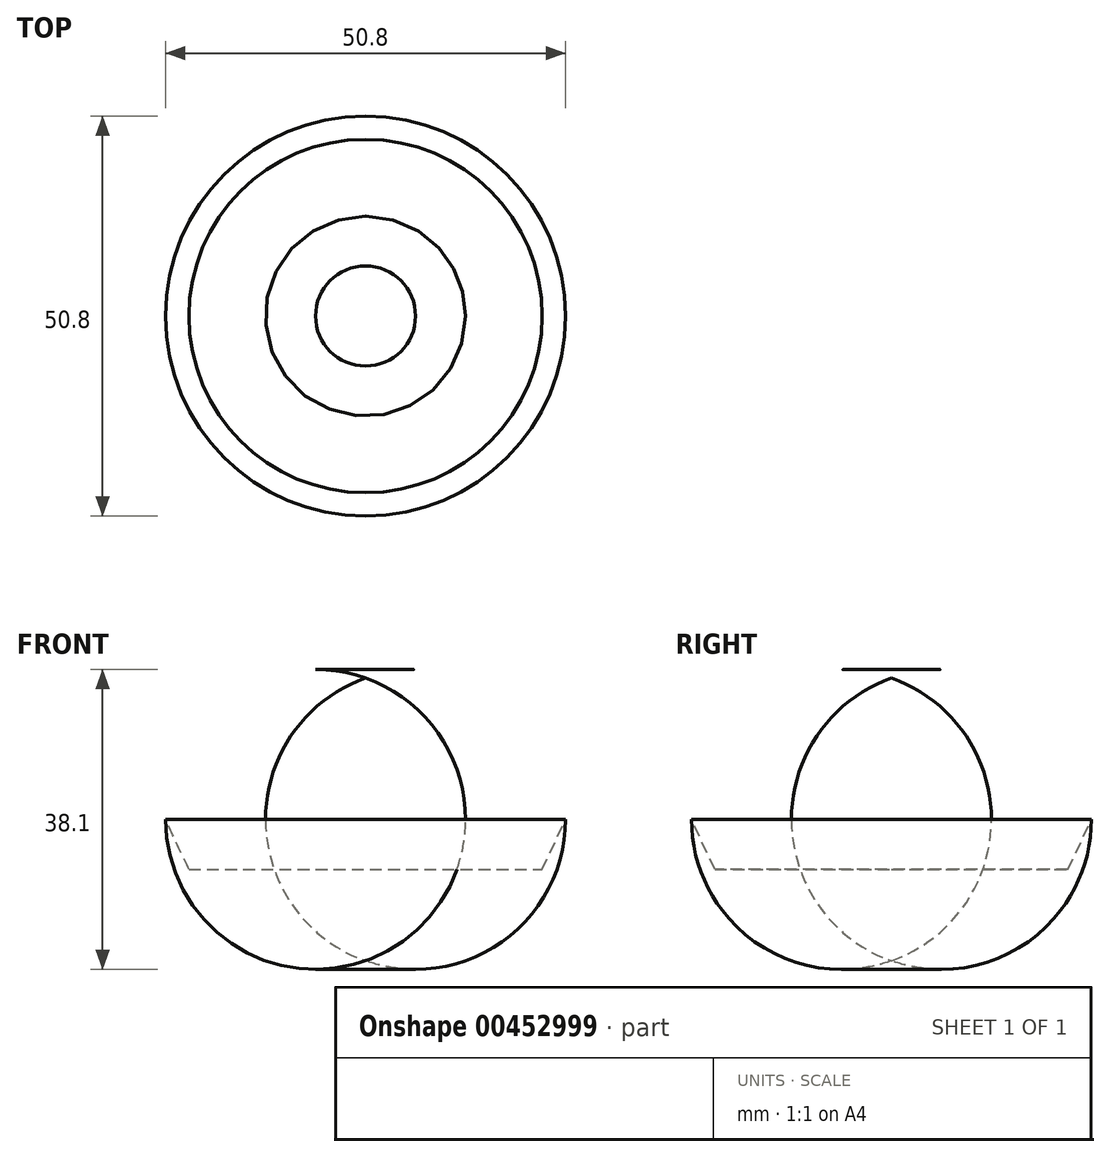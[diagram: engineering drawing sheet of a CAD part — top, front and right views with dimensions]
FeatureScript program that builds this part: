
annotation { "Feature Type Name" : "Feature", "Feature Type Description" : "" }
export const myFeature = defineFeature(function(context is Context, id is Id, definition is map)
    precondition{}
    {
        {
            var Q0;
            Q0=qCreatedBy(makeId("Front.planeOp"),FACE);
            var sketch = newSketch(context, id + "F0", { "sketchPlane" : qUnion([Q0])});
            skLineSegment(sketch, "E0.bottom", {"start": v(0, 0) * mm, "end": v(25.4, 0) * mm});
            skLineSegment(sketch, "E0.top", {"start": v(0, 25.4) * mm, "end": v(25.4, 25.4) * mm});
            skLineSegment(sketch, "E0.left", {"start": v(0, 0) * mm, "end": v(0, 25.4) * mm});
            skLineSegment(sketch, "E0.right", {"start": v(25.4, 0) * mm, "end": v(25.4, 25.4) * mm});
            skSolve(sketch);
        }
        {
            var Q0;
            Q0=makeQuery(id+"F0.imprint","IMPRINT",FACE,{"disambiguationData":[TD([[makeQuery(id+"F0.imprint","IMPRINT",EDGE,{"derivedFrom":sQuery(id+"F0.wireOp",EDGE,"E0.bottom")}),1.0]])]});
            var Q1;
            Q1=sQuery(id+"F0.wireOp",EDGE,"E0.left");
            revolve(context, id + "F1", {"entities" : qUnion([Q0]), "axis" : qUnion([Q1]), "revolveType" : RevolveType.FULL});
        }
        {
            var Q0;
            Q0=makeQuery(id+"F1.opRevolve","SWEPT_EDGE",EDGE,{"disambiguationData":[OSD([sQuery(id+"F0.wireOp",EDGE,"E0.top"),sQuery(id+"F0.wireOp",EDGE,"E0.right")])]});
            fillet(context, id + "F2", {"entities" : qUnion([Q0]), "radius" : 19.05 * mm, "tangentPropagation" : true, "allowEdgeOverflow" : false});
        }
        {
            var Q0;
            Q0=makeQuery(id+"F1.opRevolve","SWEPT_EDGE",EDGE,{"disambiguationData":[OSD([sQuery(id+"F0.wireOp",EDGE,"E0.bottom"),sQuery(id+"F0.wireOp",EDGE,"E0.right")])]});
            chamfer(context, id + "F3", {"entities" : qUnion([Q0]), "chamferType" : ChamferType.OFFSET_ANGLE, "width" : 6.35 * mm, "oppositeDirection" : true, "angle" : 25 * degree});
        }
    });
